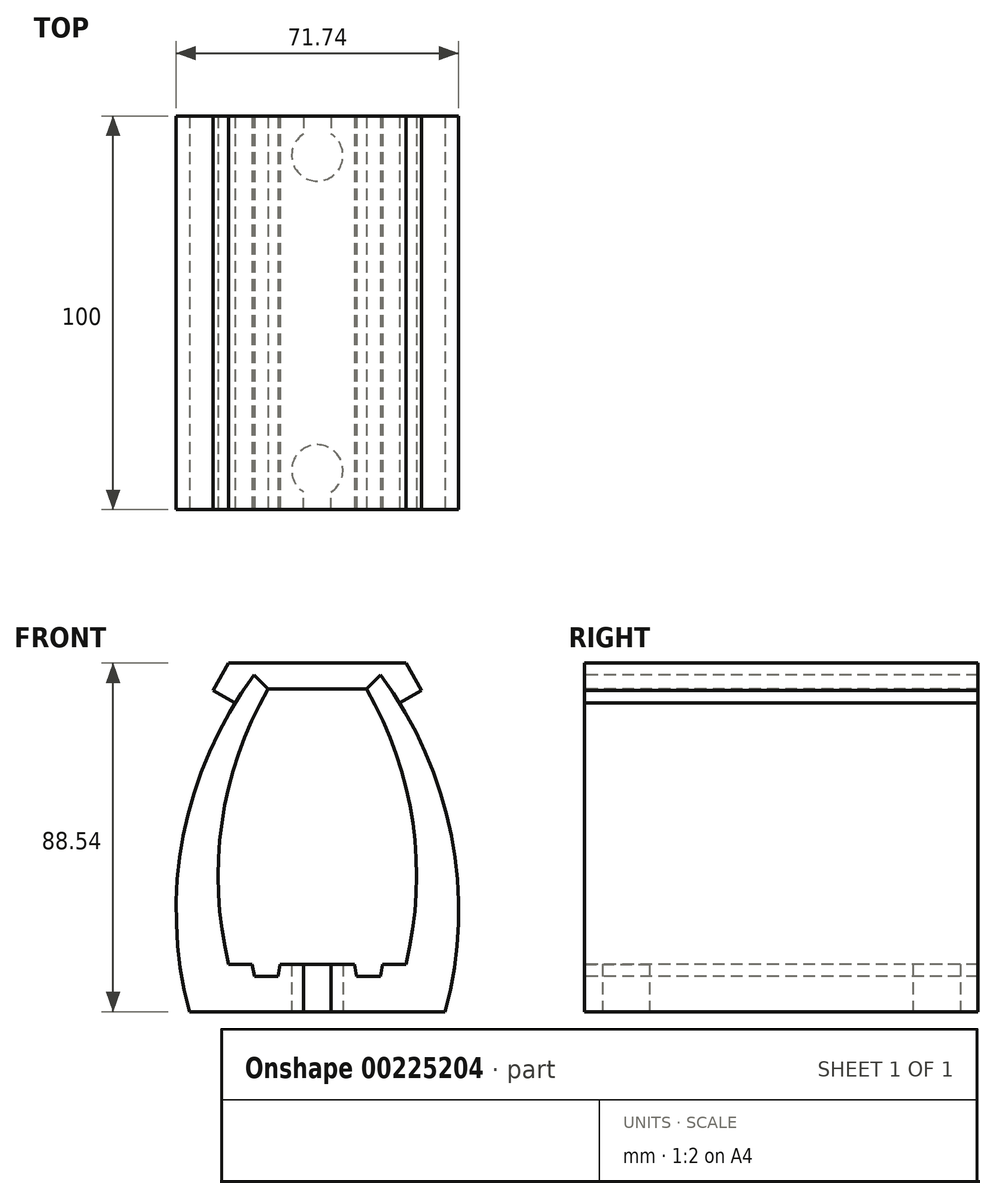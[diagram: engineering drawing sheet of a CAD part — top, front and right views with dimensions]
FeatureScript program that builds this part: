
annotation { "Feature Type Name" : "Feature", "Feature Type Description" : "" }
export const myFeature = defineFeature(function(context is Context, id is Id, definition is map)
    precondition{}
    {
        {
            var Q0;
            Q0=qCreatedBy(makeId("Front.planeOp"),FACE);
            var sketch = newSketch(context, id + "F0", { "sketchPlane" : qUnion([Q0])});
            skLineSegment(sketch, "E0", {"start": v(-22.5, 12) * mm, "end": v(-16.53, 12) * mm});
            skLineSegment(sketch, "E1", {"start": v(-16.53, 12) * mm, "end": v(-16, 9) * mm});
            skLineSegment(sketch, "E2", {"start": v(-16, 9) * mm, "end": v(-10, 9) * mm});
            skLineSegment(sketch, "E3", {"start": v(-10, 9) * mm, "end": v(-9.47, 12) * mm});
            skLineSegment(sketch, "E4.MirrorCS", {"start": v(10, 9) * mm, "end": v(9.47, 12) * mm});
            skLineSegment(sketch, "E5.MirrorCS", {"start": v(16, 9) * mm, "end": v(10, 9) * mm});
            skLineSegment(sketch, "E6.MirrorCS", {"start": v(16.53, 12) * mm, "end": v(16, 9) * mm});
            skLineSegment(sketch, "E7.MirrorCS", {"start": v(22.5, 12) * mm, "end": v(16.53, 12) * mm});
            skLineSegment(sketch, "E8", {"start": v(-9.47, 12) * mm, "end": v(9.47, 12) * mm});
            skArc(sketch, "E9", {"start": v(-12.5, 82) * mm, "mid": v(-24.26, 47.97) * mm, "end": v(-22.5, 12) * mm});
            skLineSegment(sketch, "E10", {"start": v(-12.5, 82) * mm, "end": v(-16.04, 85.54) * mm});
            skArc(sketch, "E11", {"start": v(-16.04, 85.54) * mm, "mid": v(-34.07, 44.65) * mm, "end": v(-32.5, 0) * mm});
            skArc(sketch, "E12.MirrorCS", {"start": v(12.5, 82) * mm, "mid": v(24.26, 47.97) * mm, "end": v(22.5, 12) * mm});
            skLineSegment(sketch, "E13.MirrorCS", {"start": v(12.5, 82) * mm, "end": v(16.04, 85.54) * mm});
            skArc(sketch, "E14.MirrorCS", {"start": v(16.04, 85.54) * mm, "mid": v(34.07, 44.65) * mm, "end": v(32.5, 0) * mm});
            skLineSegment(sketch, "E15", {"start": v(-32.5, 0) * mm, "end": v(32.5, 0) * mm});
            skLineSegment(sketch, "E16", {"start": v(-12.5, 82) * mm, "end": v(12.5, 82) * mm});
            skLineSegment(sketch, "E17", {"start": v(-20.9, 78.38) * mm, "end": v(-26.5, 81.6) * mm});
            skLineSegment(sketch, "E18", {"start": v(-26.5, 81.6) * mm, "end": v(-22.5, 88.54) * mm});
            skLineSegment(sketch, "E19.MirrorCS", {"start": v(26.5, 81.6) * mm, "end": v(22.5, 88.54) * mm});
            skLineSegment(sketch, "E20.MirrorCS", {"start": v(20.9, 78.38) * mm, "end": v(26.5, 81.6) * mm});
            skLineSegment(sketch, "E21", {"start": v(-22.5, 88.54) * mm, "end": v(22.5, 88.54) * mm});
            skSolve(sketch);
        }
        {
            var Q0;
            Q0=makeQuery(id+"F0.imprint","IMPRINT",FACE,{"disambiguationData":[TD([[makeQuery(id+"F0.imprint","IMPRINT",EDGE,{"derivedFrom":sQuery(id+"F0.wireOp",EDGE,"E0")}),-1.0]])]});
            extrude(context, id + "F1", {"entities" : qUnion([Q0]), "oppositeDirection" : true, "depth" : 100 * mm});
        }
        {
            var Q0;
            {var subQ4=sQuery(id+"F0.wireOp",EDGE,"E10");Q0=makeQuery(id+"F0.imprint","IMPRINT",FACE,{"disambiguationData":[TD([[makeQuery(id+"F0.imprint","IMPRINT",EDGE,{"derivedFrom":subQ4}),-1.0]])]});}
            extrude(context, id + "F2", {"entities" : qUnion([Q0]), "oppositeDirection" : true, "depth" : 100 * mm});
        }
        {
            var Q0;
            Q0=makeQuery(id+"F1.opExtrude","SWEPT_FACE",FACE,{"disambiguationData":[OSD([sQuery(id+"F0.wireOp",EDGE,"E15")])]});
            var sketch = newSketch(context, id + "F3", { "sketchPlane" : qUnion([Q0])});
            skLineSegment(sketch, "E22.0", {"start": v(-32.5, 0) * mm, "end": v(32.5, 0) * mm, "construction": true});
            skLineSegment(sketch, "E23.0", {"start": v(-32.5, -100) * mm, "end": v(32.5, -100) * mm, "construction": true});
            skLineSegment(sketch, "E24", {"start": v(0, 0) * mm, "end": v(0, -100) * mm, "construction": true});
            skLineSegment(sketch, "E25", {"start": v(0, -50) * mm, "end": v(-10.86, -50) * mm, "construction": true});
            skArc(sketch, "E26", {"start": v(-3.5, -4.52) * mm, "mid": v(0, -16.5) * mm, "end": v(3.5, -4.52) * mm});
            skLineSegment(sketch, "E27.bottom", {"start": v(-3.5, 0) * mm, "end": v(3.5, 0) * mm});
            skLineSegment(sketch, "E27.left", {"start": v(-3.5, 0) * mm, "end": v(-3.5, -4.52) * mm});
            skLineSegment(sketch, "E27.right", {"start": v(3.5, 0) * mm, "end": v(3.5, -4.52) * mm});
            skPoint(sketch, "E27.middle", {"position": v(0, -3.02) * mm});
            skPoint(sketch, "E28.orphan", {"position": v(-3.5, -6.05) * mm});
            skPoint(sketch, "E29.orphan", {"position": v(3.5, -6.05) * mm});
            skLineSegment(sketch, "E30.MirrorCS", {"start": v(-3.5, -100) * mm, "end": v(-3.5, -95.48) * mm});
            skArc(sketch, "E31.MirrorCS", {"start": v(-3.5, -95.48) * mm, "mid": v(0, -83.5) * mm, "end": v(3.5, -95.48) * mm});
            skLineSegment(sketch, "E32.MirrorCS", {"start": v(3.5, -100) * mm, "end": v(3.5, -95.48) * mm});
            skLineSegment(sketch, "E33", {"start": v(-3.5, -100) * mm, "end": v(3.5, -100) * mm});
            skSolve(sketch);
        }
        {
            var Q0;
            Q0=makeQuery(id+"F3.imprint","IMPRINT",FACE,{"disambiguationData":[TD([[makeQuery(id+"F3.imprint","IMPRINT",EDGE,{"derivedFrom":sQuery(id+"F3.wireOp",EDGE,"E26")}),1.0]])]});
            var Q1;
            Q1=makeQuery(id+"F3.imprint","IMPRINT",FACE,{"disambiguationData":[TD([[makeQuery(id+"F3.imprint","IMPRINT",EDGE,{"derivedFrom":sQuery(id+"F3.wireOp",EDGE,"E30.MirrorCS")}),-1.0]])]});
            extrude(context, id + "F4", {"entities" : qUnion([Q0, Q1]), "operationType" : NewBodyOperationType.REMOVE, "oppositeDirection" : true, "depth" : 25 * mm});
        }
    });
